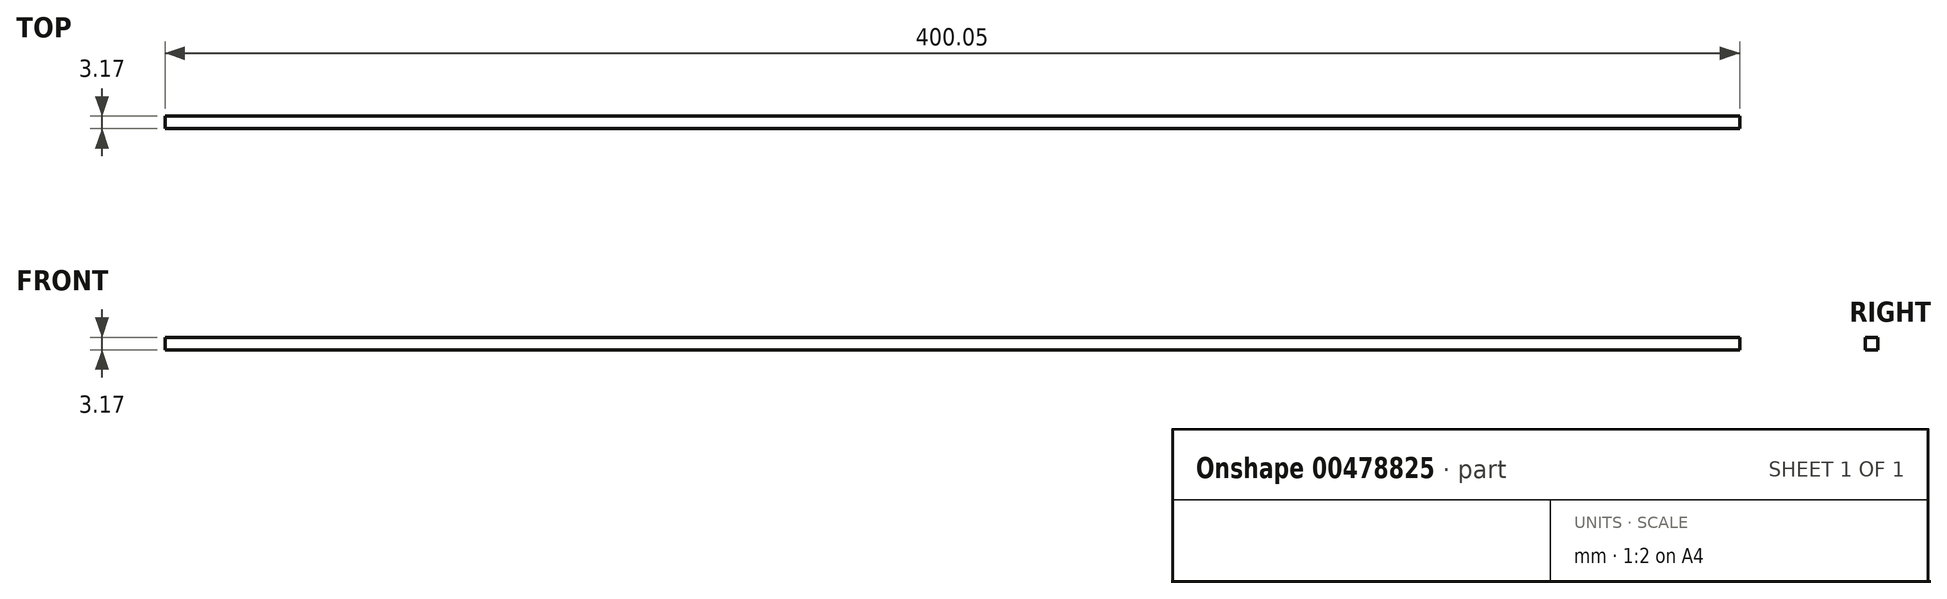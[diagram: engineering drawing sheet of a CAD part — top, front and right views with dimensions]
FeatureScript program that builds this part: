
annotation { "Feature Type Name" : "Feature", "Feature Type Description" : "" }
export const myFeature = defineFeature(function(context is Context, id is Id, definition is map)
    precondition{}
    {
        {
            var Q0;
            Q0=qCreatedBy(makeId("Top.planeOp"),FACE);
            var sketch = newSketch(context, id + "F0", { "sketchPlane" : qUnion([Q0])});
            skLineSegment(sketch, "E0.bottom", {"start": v(-863.6, 0) * mm, "end": v(-463.55, 0) * mm});
            skLineSegment(sketch, "E0.top", {"start": v(-863.6, -3.18) * mm, "end": v(-463.55, -3.18) * mm});
            skLineSegment(sketch, "E0.left", {"start": v(-863.6, 0) * mm, "end": v(-863.6, -3.18) * mm});
            skLineSegment(sketch, "E0.right", {"start": v(-463.55, 0) * mm, "end": v(-463.55, -3.18) * mm});
            skSolve(sketch);
        }
        {
            var Q0;
            Q0=makeQuery(id+"F0.imprint","IMPRINT",FACE,{"disambiguationData":[TD([[makeQuery(id+"F0.imprint","IMPRINT",EDGE,{"derivedFrom":sQuery(id+"F0.wireOp",EDGE,"E0.bottom")}),-1.0]])]});
            extrude(context, id + "F1", {"entities" : qUnion([Q0]), "depth" : 3.17 * mm});
        }
    });
